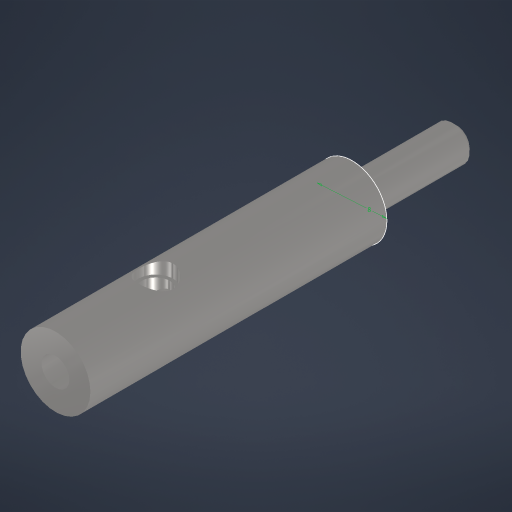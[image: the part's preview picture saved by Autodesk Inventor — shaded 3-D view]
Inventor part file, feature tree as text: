
AUTODESK INVENTOR PART (.ipt)
format: ipt  version: 2023 (Build 270158000, 158)  size: 224,768 bytes
history: native  units: mm
features: sketch x5, extrude x3, hole x3, plane x3, chamfer x1
ambient origin geometry x8: Origin, YZ Plane, XZ Plane, XY Plane, X Axis, Y Axis, Z Axis, Center Point
bodies: Solid1 (feature_tree)
feature tree (15):
  extrude  "Extrusion1"  Depth=34.0mm TaperAngle=0.0deg
  extrude  "Extrusion2"  Depth=2.0mm TaperAngle=0.0deg
  chamfer  "Chamfer1"  Distance=2.0mm Angle=45.0deg
  hole  "Hole1"  [1 undecoded]
  plane  "Work Plane1"
  plane  "Work Plane2"
  extrude  "Extrusion3"  Depth=9.5mm
  plane  "Work Plane3"
  sketch  "Sketch6"  dims[d21=1.5mm d22=100.0mm d23=0.0mm d24=4.0mm d25=11.5mm d26=4.0mm d27=6.0mm d28=4.0mm d29=2.0mm d30=90.0deg d31=1.5mm d32=0.0mm d33=3.2mm d34=6.0mm d35=4.0mm d36=2.0mm d37=90.0deg d38=4.0mm d39=20.594885mm]
  hole  "Hole2"  [1 undecoded]
  hole  "Hole3"  [1 undecoded]
  sketch  "Sketch1"  dims[d0=8.0mm d1=34.0mm d2=0.0mm]
  sketch  "Sketch2"  dims[d3=4.0mm d4=12.0mm d5=0.0mm d6=0.5mm d7=2.0mm d8=45.0deg]
  sketch  "Sketch3"  dims[d9=3.2mm d10=6.0mm d11=4.0mm d12=2.0mm d13=90.0deg d14=14.0mm d15=20.594885mm d18=0.0mm]
  sketch  "Sketch5"  dims[d19=12.0mm d20=9.5mm]
note: 3 required parameter values undecoded (feature->parameter linkage not recoverable at this tier; creation-order binding heuristic only, values carry confidence <= 0.55)
